# Revit family: S-tank_ET
name_source: partatom
category: Оборудование
units: mm (PartAtom-declared; Revit-internal decimal feet)

## family parameters
Всегда вертикально = Да
Классификация = Нет
На основе рабочей плоскости = Нет
Общий = Нет
При загрузке вырезать с полостями = Нет
Размер круглого соединителя = Использовать диаметр
Тип детали = Нормальный
Точка расчета площади = Нет

## types (9) — shared parameters
ADSK_URL документации изделия = http://s-tank.ru
ADSK_Группирование = Оборудование
ADSK_Единица измерения = шт.
ADSK_Завод-изготовитель = ООО “С-ТЭНК ВОТЕР ХИТЕРС”
ADSK_Наименование = Буферная емкость
DN1 = 40 мм
DN2 = 15 мм
shrf = 18 мм

## per-type parameters (varying)
| type | A | ADSK_Код изделия | ADSK_Марка | ADSK_Масса | B | C | D | E | H | I | a | Диаметрсизоляцией |
| ET300 | 125 мм | 1.2001 | ET 300 | 65 | 230 мм | 390 мм | 550 мм | 1190 мм | 1600 мм | 1350 мм | 105 мм | 630 мм |
| ET500 | 122 мм | 1.2002 | ET 500 | 87 | 225 мм | 385 мм | 545 мм | 1185 мм | 1605 мм | 1345 мм | 130 мм | 780 мм |
| ET750 | 117 мм | 1.2003 | ET 750 | 103 | 215 мм | 375 мм | 535 мм | 1175 мм | 1630 мм | 1335 мм | 153 мм | 920 мм |
| ET1000 | 117 мм | 1.2004 | ET 1000 | 131 | 205 мм | 450 мм | 695 мм | 1675 мм | 2205 мм | 1920 мм | 153 мм | 920 мм |
| ET1200 | 177 мм | 1.2005 | ET 1200 | 174 | 265 мм | 455 мм | 645 мм | 1475 мм | 2080 мм | 1665 мм | 178 мм | 1070 мм |
| ET1500 | 177 мм | 1.2006 | ET 1500 | 200 | 265 мм | 505 мм | 745 мм | 1775 мм | 2370 мм | 2015 мм | 178 мм | 1070 мм |
| ET2000 | 250 мм | 1.2007 | ET 2000 | 246 | 350 мм | 540 мм | 730 мм | 1560 мм | 2100 мм | 1750 мм | 225 мм | 1350 мм |
| ET3000 | 332 мм | 1.2008 | ET 3000 | 450 | 465 мм | 655 мм | 845 мм | 1675 мм | 2315 мм | 1865 мм | 272 мм | 1630 мм |
| ET5000 | 332 мм | 1.2009 | ET 5000 | 615 | 465 мм | 765 мм | 1065 мм | 2315 мм | 2315 мм | 2615 мм | 272 мм | 1630 мм |

note: column(s) folded — value = type name in every type: ADSK_Обозначение
